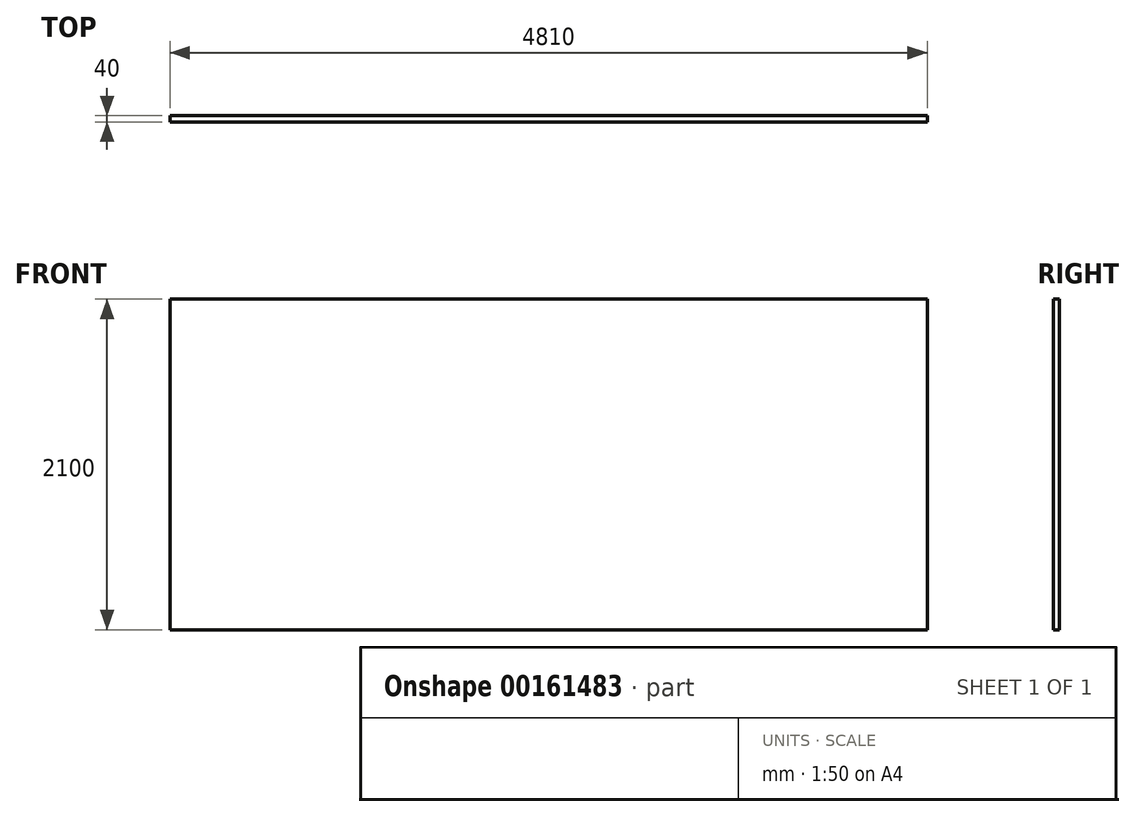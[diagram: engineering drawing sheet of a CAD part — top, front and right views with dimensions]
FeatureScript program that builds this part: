
annotation { "Feature Type Name" : "Feature", "Feature Type Description" : "" }
export const myFeature = defineFeature(function(context is Context, id is Id, definition is map)
    precondition{}
    {
        {
            var Q0;
            Q0=qCreatedBy(makeId("Front.planeOp"),FACE);
            var sketch = newSketch(context, id + "F0", { "sketchPlane" : qUnion([Q0])});
            skLineSegment(sketch, "E0.bottom", {"start": v(-2405, 1050) * mm, "end": v(2405, 1050) * mm});
            skLineSegment(sketch, "E0.top", {"start": v(-2405, -1050) * mm, "end": v(2405, -1050) * mm});
            skLineSegment(sketch, "E0.left", {"start": v(-2405, 1050) * mm, "end": v(-2405, -1050) * mm});
            skLineSegment(sketch, "E0.right", {"start": v(2405, 1050) * mm, "end": v(2405, -1050) * mm});
            skPoint(sketch, "E0.middle", {"position": v(0, 0) * mm});
            skSolve(sketch);
        }
        {
            var Q0;
            Q0 = qSketchRegion(id + "F0", true);
            extrude(context, id + "F1", {"entities" : qUnion([Q0]), "endBound" : BoundingType.SYMMETRIC, "depth" : 40 * mm, "offsetDistance" : 25 * mm});
        }
    });
